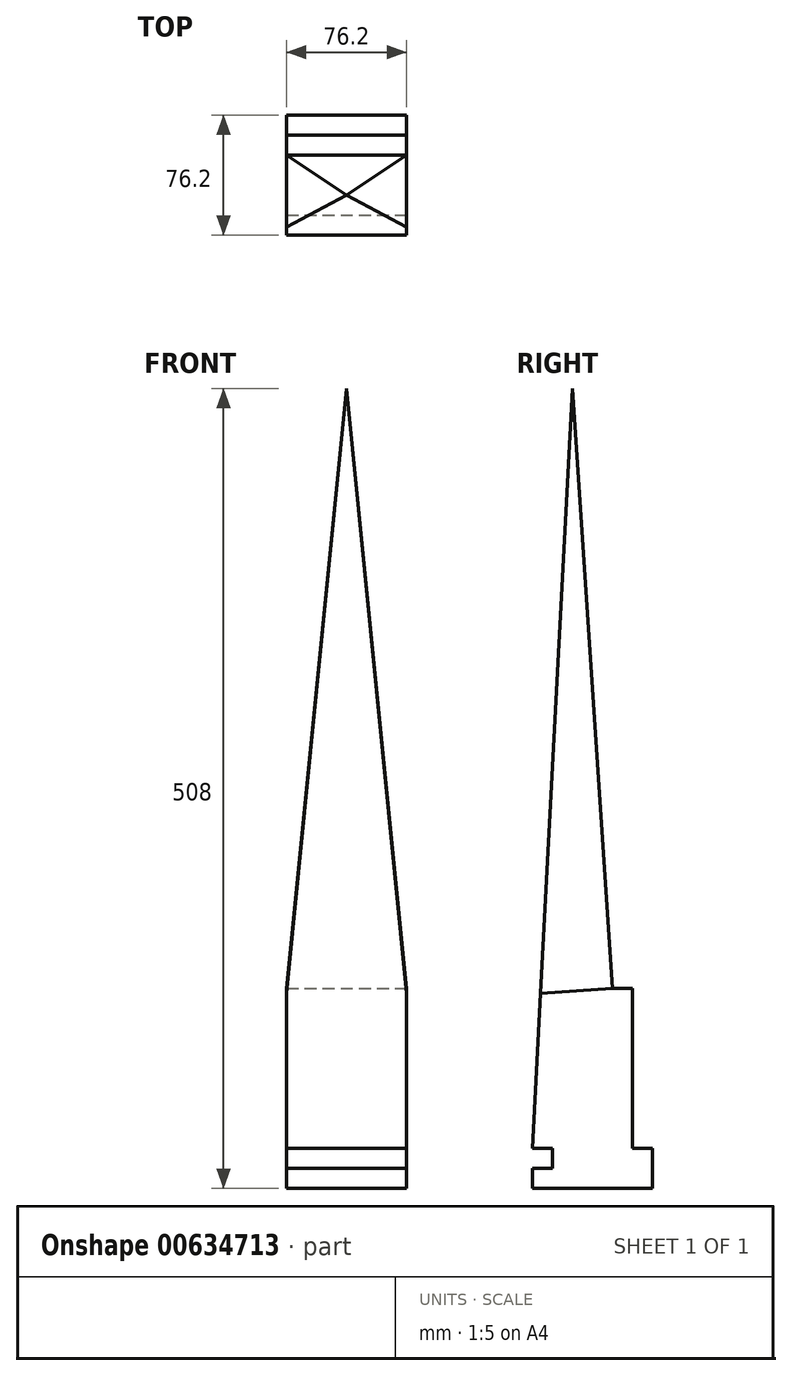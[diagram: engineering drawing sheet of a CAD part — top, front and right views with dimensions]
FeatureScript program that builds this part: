
annotation { "Feature Type Name" : "Feature", "Feature Type Description" : "" }
export const myFeature = defineFeature(function(context is Context, id is Id, definition is map)
    precondition{}
    {
        {
            var Q0;
            Q0=qCreatedBy(makeId("Top.planeOp"),FACE);
            var sketch = newSketch(context, id + "F0", { "sketchPlane" : qUnion([Q0])});
            skLineSegment(sketch, "E0.bottom", {"start": v(38.1, 38.1) * mm, "end": v(-38.1, 38.1) * mm});
            skLineSegment(sketch, "E0.top", {"start": v(38.1, -38.1) * mm, "end": v(-38.1, -38.1) * mm});
            skLineSegment(sketch, "E0.left", {"start": v(38.1, 38.1) * mm, "end": v(38.1, -38.1) * mm});
            skLineSegment(sketch, "E0.right", {"start": v(-38.1, 38.1) * mm, "end": v(-38.1, -38.1) * mm});
            skPoint(sketch, "E0.middle", {"position": v(0, 0) * mm});
            skSolve(sketch);
        }
        {
            var Q0;
            Q0=makeQuery(id+"F0.imprint","IMPRINT",FACE,{"disambiguationData":[TD([[makeQuery(id+"F0.imprint","IMPRINT",EDGE,{"derivedFrom":sQuery(id+"F0.wireOp",EDGE,"E0.bottom")}),1.0]])]});
            extrude(context, id + "F1", {"entities" : qUnion([Q0]), "depth" : 25.4 * mm, "offsetDistance" : 25.4 * mm});
        }
        {
            var Q0;
            Q0=makeQuery(id+"F1.opExtrude","CAP_FACE",FACE,{"disambiguationData":[OSD([sQuery(id+"F0.wireOp",EDGE,"E0.bottom"),sQuery(id+"F0.wireOp",EDGE,"E0.top"),sQuery(id+"F0.wireOp",EDGE,"E0.left"),sQuery(id+"F0.wireOp",EDGE,"E0.right")])],"isStart":false});
            var sketch = newSketch(context, id + "F2", { "sketchPlane" : qUnion([Q0])});
            skLineSegment(sketch, "E1", {"start": v(-38.1, 12.7) * mm, "end": v(38.1, 12.7) * mm});
            skLineSegment(sketch, "E2", {"start": v(-38.1, 25.4) * mm, "end": v(38.1, 25.4) * mm});
            skSolve(sketch);
        }
        {
            var Q0;
            {var subQ0=sQuery(id+"F2.wireOp",EDGE,"E1");Q0=makeQuery(id+"F2.imprint","IMPRINT",FACE,{"disambiguationData":[TD([[makeQuery(id+"F2.imprint","IMPRINT",EDGE,{"derivedFrom":subQ0}),1.0]])]});}
            extrude(context, id + "F3", {"entities" : qUnion([Q0]), "operationType" : NewBodyOperationType.ADD, "depth" : 101.6 * mm, "offsetDistance" : 25.4 * mm});
        }
        {
            var Q0;
            Q0=qCreatedBy(makeId("Right.planeOp"),FACE);
            var sketch = newSketch(context, id + "F4", { "sketchPlane" : qUnion([Q0])});
            skLineSegment(sketch, "E3.0.0", {"start": v(-38.1, 0) * mm, "end": v(38.1, 0) * mm});
            skLineSegment(sketch, "E3.0.1", {"start": v(38.1, 0) * mm, "end": v(38.1, 25.4) * mm});
            skLineSegment(sketch, "E3.0.2", {"start": v(38.1, 25.4) * mm, "end": v(25.4, 25.4) * mm});
            skLineSegment(sketch, "E3.0.3", {"start": v(25.4, 25.4) * mm, "end": v(25.4, 127) * mm});
            skLineSegment(sketch, "E3.0.4", {"start": v(25.4, 127) * mm, "end": v(12.7, 127) * mm});
            skLineSegment(sketch, "E3.0.5", {"start": v(12.7, 127) * mm, "end": v(12.7, 25.4) * mm});
            skLineSegment(sketch, "E3.0.6", {"start": v(12.7, 25.4) * mm, "end": v(-38.1, 25.4) * mm});
            skLineSegment(sketch, "E3.0.7", {"start": v(-38.1, 25.4) * mm, "end": v(-38.1, 0) * mm});
            skLineSegment(sketch, "E4", {"start": v(-12.7, 0) * mm, "end": v(-12.7, 25.4) * mm, "construction": true});
            skLineSegment(sketch, "E5", {"start": v(12.7, 127) * mm, "end": v(-12.7, 508) * mm});
            skLineSegment(sketch, "E6", {"start": v(-12.7, 508) * mm, "end": v(-38.1, 25.4) * mm});
            skSolve(sketch);
        }
        {
            var Q0;
            {var subQ0=sQuery(id+"F0.wireOp",EDGE,"E0.left");Q0=makeQuery(id+"F3.boolean.opBoolean","MERGE",FACE,{"derivedFrom":[makeQuery(id+"F1.opExtrude","SWEPT_FACE",FACE,{"disambiguationData":[OSD([subQ0])]}),makeQuery(id+"F3.opExtrude","SWEPT_FACE",FACE,{"disambiguationData":[OSD([subQ0])]})]});}
            var sketch = newSketch(context, id + "F5", { "sketchPlane" : qUnion([Q0])});
            skLineSegment(sketch, "E7.0.0", {"start": v(12.7, 25.4) * mm, "end": v(12.7, 127) * mm});
            skLineSegment(sketch, "E7.0.1", {"start": v(12.7, 127) * mm, "end": v(-12.7, 508) * mm});
            skLineSegment(sketch, "E7.0.2", {"start": v(-12.7, 508) * mm, "end": v(-38.1, 25.4) * mm});
            skLineSegment(sketch, "E7.0.3", {"start": v(-38.1, 25.4) * mm, "end": v(12.7, 25.4) * mm});
            skSolve(sketch);
        }
        {
            var Q0;
            Q0=makeQuery(id+"F5.imprint","IMPRINT",FACE,{"disambiguationData":[TD([[makeQuery(id+"F5.imprint","IMPRINT",EDGE,{"derivedFrom":sQuery(id+"F5.wireOp",EDGE,"E7.0.0")}),-1.0]])]});
            var Q1;
            {var subQ0=sQuery(id+"F0.wireOp",EDGE,"E0.right");Q1=makeQuery(id+"F3.boolean.opBoolean","MERGE",FACE,{"derivedFrom":[makeQuery(id+"F1.opExtrude","SWEPT_FACE",FACE,{"disambiguationData":[OSD([subQ0])]}),makeQuery(id+"F3.opExtrude","SWEPT_FACE",FACE,{"disambiguationData":[OSD([subQ0])]})]});}
            extrude(context, id + "F6", {"entities" : qUnion([Q0]), "operationType" : NewBodyOperationType.ADD, "endBound" : BoundingType.UP_TO_SURFACE, "oppositeDirection" : true, "depth" : 25.4 * mm, "endBoundEntityFace" : qUnion([Q1]), "offsetDistance" : 25.4 * mm});
        }
        {
            var Q0;
            {var subQ0=sQuery(id+"F0.wireOp",EDGE,"E0.left");Q0=makeQuery(id+"F6.boolean.opBoolean","MERGE",FACE,{"derivedFrom":[makeQuery(id+"F3.boolean.opBoolean","MERGE",FACE,{"derivedFrom":[makeQuery(id+"F1.opExtrude","SWEPT_FACE",FACE,{"disambiguationData":[OSD([subQ0])]}),makeQuery(id+"F3.opExtrude","SWEPT_FACE",FACE,{"disambiguationData":[OSD([subQ0])]})]}),makeQuery(id+"F6.opExtrude","CAP_FACE",FACE,{"disambiguationData":[OSD([sQuery(id+"F5.wireOp",EDGE,"E7.0.0"),sQuery(id+"F5.wireOp",EDGE,"E7.0.1"),sQuery(id+"F5.wireOp",EDGE,"E7.0.2"),sQuery(id+"F5.wireOp",EDGE,"E7.0.3")])],"isStart":true})]});}
            var sketch = newSketch(context, id + "F7", { "sketchPlane" : qUnion([Q0])});
            skLineSegment(sketch, "E8", {"start": v(-38.1, 25.4) * mm, "end": v(-25.4, 25.4) * mm});
            skLineSegment(sketch, "E9", {"start": v(-25.4, 25.4) * mm, "end": v(-25.4, 12.7) * mm});
            skLineSegment(sketch, "E10", {"start": v(-25.4, 12.7) * mm, "end": v(-38.1, 12.7) * mm});
            skSolve(sketch);
        }
        {
            var Q0;
            {var subQ0=sQuery(id+"F7.wireOp",EDGE,"E8");Q0=makeQuery(id+"F7.imprint","IMPRINT",FACE,{"disambiguationData":[TD([[makeQuery(id+"F7.imprint","IMPRINT",EDGE,{"derivedFrom":subQ0}),-1.0]])]});}
            extrude(context, id + "F8", {"entities" : qUnion([Q0]), "operationType" : NewBodyOperationType.REMOVE, "endBound" : BoundingType.THROUGH_ALL, "oppositeDirection" : true, "depth" : 25.4 * mm, "offsetDistance" : 25.4 * mm});
        }
        {
            var Q0;
            Q0=makeQuery(id+"F6.opExtrude","SWEPT_FACE",FACE,{"disambiguationData":[OSD([sQuery(id+"F5.wireOp",EDGE,"E7.0.1")])]});
            var sketch = newSketch(context, id + "F9", { "sketchPlane" : qUnion([Q0])});
            skPoint(sketch, "E11", {"position": v(0, 507.72) * mm});
            skLineSegment(sketch, "E12", {"start": v(0, 507.72) * mm, "end": v(38.1, 125.87) * mm});
            skLineSegment(sketch, "E13", {"start": v(0, 507.72) * mm, "end": v(-38.1, 125.87) * mm});
            skSolve(sketch);
        }
        {
            var Q0;
            {var subQ0=sQuery(id+"F9.wireOp",EDGE,"E13");Q0=makeQuery(id+"F9.imprint","IMPRINT",FACE,{"disambiguationData":[TD([[makeQuery(id+"F9.imprint","IMPRINT",EDGE,{"derivedFrom":subQ0}),-1.0]])]});}
            extrude(context, id + "F10", {"entities" : qUnion([Q0]), "operationType" : NewBodyOperationType.REMOVE, "endBound" : BoundingType.THROUGH_ALL, "oppositeDirection" : true, "depth" : 25.4 * mm, "offsetDistance" : 25.4 * mm});
        }
        {
            var Q0;
            Q0=makeQuery(id+"F6.opExtrude","SWEPT_FACE",FACE,{"disambiguationData":[OSD([sQuery(id+"F5.wireOp",EDGE,"E7.0.1")])]});
            var sketch = newSketch(context, id + "F11", { "sketchPlane" : qUnion([Q0])});
            skLineSegment(sketch, "E14", {"start": v(0, 507.72) * mm, "end": v(38.1, 125.87) * mm});
            skSolve(sketch);
        }
        {
            var Q0;
            Q0=makeQuery(id+"F11.imprint","IMPRINT",FACE,{"disambiguationData":[TD([[makeQuery(id+"F11.imprint","IMPRINT",EDGE,{"derivedFrom":sQuery(id+"F11.wireOp",EDGE,"E14")}),1.0]])]});
            extrude(context, id + "F12", {"entities" : qUnion([Q0]), "operationType" : NewBodyOperationType.REMOVE, "endBound" : BoundingType.THROUGH_ALL, "oppositeDirection" : true, "depth" : 25.4 * mm, "offsetDistance" : 25.4 * mm});
        }
    });
